# Revit family: 6c7b14ed-cf5b-4825-9b4a-d050c93f193f
name_source: partatom
category: Plumbing Fixtures
revit_build: Autodesk Revit 2016 (Build: 20161004_0715(x64)
units: mm (PartAtom-declared; Revit-internal decimal feet)

## family parameters
Always vertical = Yes
Cut with Voids When Loaded = No
Part Type = Normal
Room Calculation Point = No
Round Connector Dimension = Use Radius
Shared = No
Work Plane-Based = No

## types (1)
- 6c7b14ed-cf5b-4825-9b4a-d050c93f193f
    ADA Compliant = Yes
    CW Connection = Yes
    Cold Water Connection Diameter = 0' - 0 3/8"
    Cold Water Connection Radius = 0' - 0 3/16"
    Default Elevation = 0' - 0"
    Description = Kelston™ Comfort Height® two-piece 1.6 gpf elongated toilet
    Flushing System = Class Five®
    Gallons Per Flush = 1.6
    HW Connection = No
    Liters Per Flush = 6
    Manufacturer = Kohler
    Material = Vitreous China
    Model = K-3754
    Overall Height = 2' - 6 1/2"
    Overall Length = 2' - 6"
    Overall Width = 1' - 4 3/4"
    Rough-in = 1' - 0"
    Seat = Order Separately
    URL = http://www.us.kohler.com
    Vent Connection = No
    Waste Connection = Yes
    Waste Connection Diameter = 0' - 3"
    Waste Connection Radius = 0' - 1 1/2"

## geometry (parser evidence)
native form markers: Sweep x6
no freeform markers — native parametric forms only
